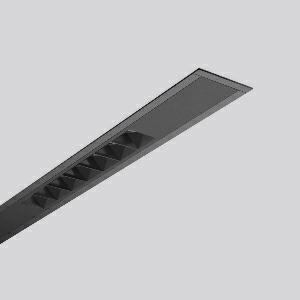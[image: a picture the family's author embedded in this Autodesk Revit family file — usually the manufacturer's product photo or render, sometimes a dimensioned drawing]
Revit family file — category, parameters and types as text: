
# Revit family: less_is_more_beamline_312471_003_1_94e0
name_source: partatom
category: Lighting Fixtures
units: mm (PartAtom-declared; Revit-internal decimal feet)

## family parameters
Cut with Voids When Loaded = No
Host = Face
Light Source = No
Part Type = Normal
Room Calculation Point = No
Round Connector Dimension = Use Diameter
Shared = No

## types (1)
- LESS IS MORE BEAMLINE (1 x LED Modul 940, 1083.33 lm, 4000)
    Apparent Load = 35 VA
    CIE Flux Codes = 100 100 100 100 100
    Color Rendering = 92
    Color Temperature = 4000
    Default Elevation = 1800 mm
    Description = Series: LESS IS MORE BEAMLINE
Linear recessed ceiling and wall luminaire for aesthetically sophisticated lighting. Luminaire with three LED light units. Housing: extruded aluminium profile, powder-coated. End cap aluminium powder-coated. LED light unit with MRS technology: Mini-Reflector-System made of metallised thermoplastic with prismatic black glare-suppressing frame for pleasant glare-free light (RUG < 10). Each LED light unit has 7 reflector elements. Narrow beam light distribution. Ceiling installation with pre-assembled SBS mounting system. LED unit with integrated converter interchangeable and removable. Suitable for through-wiring. 
Colour: deep black, matt (RAL 9005)
Length: 1702 mm
Width: 71 mm
Height: 1.5 mm
Cut-out length: 1688 mm
Cut-out width: 60 mm
Recess height: 125 mm
Luminaire: recess height: 106 mm
Lamp: LED
Socket: without socket
Colour temperature: 4000K
Colour rendering index (CRI): 90
System power: 35 W
Rated luminous flux: 3250 lm
Luminous efficiency: 93 lm/W
Control gear: Regulated power supply
Protection class: I
Type of protection: IP 20
    Height = 0 mm  [stored 0 ft]
    Lamp = 1 x LED Modul 940
    Lamp Light Flux = 1083.33 lm
    Lamp count = 1
    Length = 1702 mm
    Lifetime = 50000 h
    Luminous efficacy = 93 lm/W
    Manufacturer = RZB
    ModVariant = No
    Model = 312471.003.1
    Mounting Place = Ceiling, Wall
    Mounting Type = Recessed
    Number of Poles = 1
    OnlyDefault = Yes
    Power Factor = 1
    Product Name = LESS IS MORE BEAMLINE
    Product group = Recessed LED linear luminaires
    ProductGroupID = 407
    Protection Class = Protection class I
    Protection Degree = IP 20
    RLX_Detail_Level = 1
    RLX_Emergency_Light_Flux = 0 lm
    RLX_Emergency_Type = 0
    RLX_Emergency_Type_DB = No
    RlxData = <blob elided: 24245 chars, md5=3b9d809c>
    Socket = socket
    Standby Power = 0 W
    System Light Flux = 3250 lm
    System Power = 35 W
    Type Comments = Product without accessories
    Type Image = 312465.003.jpg
    URL = http://relux.com
    VarID = ---
    Voltage = 230 V
    Voltage Range = 220-240 V
    Weight = 0.00 kg
    Width = 71 mm

note: [stored X ft] marks values corroborated as IEEE doubles in the binary element streams (Revit-internal decimal feet)

## geometry (parser evidence)
native form markers: Blend x4, Sweep x17
no freeform markers — native parametric forms only
